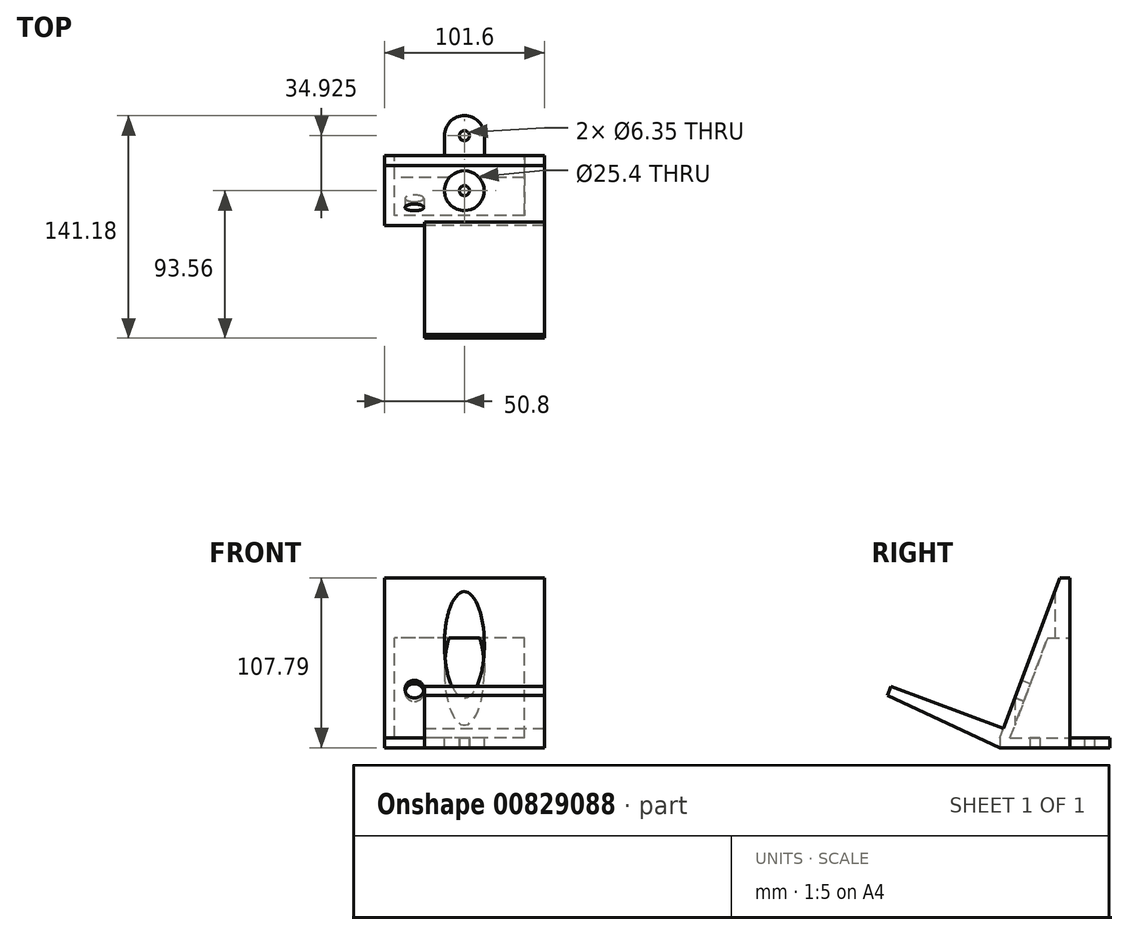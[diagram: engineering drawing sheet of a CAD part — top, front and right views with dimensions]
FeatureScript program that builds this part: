
annotation { "Feature Type Name" : "Feature", "Feature Type Description" : "" }
export const myFeature = defineFeature(function(context is Context, id is Id, definition is map)
    precondition{}
    {
        {
            var Q0;
            Q0=qCreatedBy(makeId("Right.planeOp"),FACE);
            var sketch = newSketch(context, id + "F0", { "sketchPlane" : qUnion([Q0])});
            skLineSegment(sketch, "E0.top", {"start": v(-30.3, 41.28) * mm, "end": v(14.14, 41.28) * mm});
            skLineSegment(sketch, "E0.left", {"start": v(-30.3, 47.63) * mm, "end": v(-30.3, 41.28) * mm});
            skLineSegment(sketch, "E0.right", {"start": v(14.14, 47.47) * mm, "end": v(14.14, 41.28) * mm});
            skLineSegment(sketch, "E1.top", {"start": v(14.14, 149.07) * mm, "end": v(7.8, 149.07) * mm});
            skLineSegment(sketch, "E1.left", {"start": v(14.14, 47.47) * mm, "end": v(14.14, 149.07) * mm});
            skLineSegment(sketch, "E2.left", {"start": v(14.14, 41.28) * mm, "end": v(14.14, 47.63) * mm});
            skLineSegment(sketch, "E3", {"start": v(-30.3, 47.63) * mm, "end": v(7.8, 149.07) * mm});
            skLineSegment(sketch, "E4", {"start": v(-5.62, 113.36) * mm, "end": v(0.33, 111.13) * mm, "construction": true});
            skLineSegment(sketch, "E5", {"start": v(-30.3, 47.63) * mm, "end": v(-101.64, 74.43) * mm});
            skLineSegment(sketch, "E6", {"start": v(-101.64, 74.43) * mm, "end": v(-99.4, 80.37) * mm});
            skLineSegment(sketch, "E7", {"start": v(-99.4, 80.37) * mm, "end": v(-28.07, 53.58) * mm});
            skLineSegment(sketch, "E8", {"start": v(-101.64, 74.43) * mm, "end": v(-30.3, 41.28) * mm});
            skLineSegment(sketch, "E9", {"start": v(-23.72, 47.63) * mm, "end": v(0.13, 111.13) * mm});
            skLineSegment(sketch, "E10", {"start": v(0.13, 111.13) * mm, "end": v(7.8, 111.13) * mm});
            skLineSegment(sketch, "E11", {"start": v(7.8, 111.13) * mm, "end": v(7.8, 47.63) * mm});
            skLineSegment(sketch, "E12", {"start": v(7.8, 47.63) * mm, "end": v(-23.72, 47.63) * mm});
            skLineSegment(sketch, "E13", {"start": v(-11.58, 47.63) * mm, "end": v(-11.58, 41.28) * mm, "construction": true});
            skLineSegment(sketch, "E14", {"start": v(7.8, 79.38) * mm, "end": v(14.14, 79.38) * mm, "construction": true});
            skSolve(sketch);
        }
        {
            var Q0;
            Q0=makeQuery(id+"F0.imprint","IMPRINT",FACE,{"disambiguationData":[TD([[makeQuery(id+"F0.imprint","IMPRINT",EDGE,{"derivedFrom":sQuery(id+"F0.wireOp",EDGE,"E1.bottom")}),-1.0]])]});
            var Q1;
            Q1=makeQuery(id+"F0.imprint","IMPRINT",FACE,{"disambiguationData":[TD([[makeQuery(id+"F0.imprint","IMPRINT",EDGE,{"derivedFrom":sQuery(id+"F0.wireOp",EDGE,"E0.top")}),1.0]])]});
            extrude(context, id + "F1", {"entities" : qUnion([Q0, Q1]), "depth" : 101.6 * mm, "offsetDistance" : 25.4 * mm});
        }
        {
            var Q0;
            Q0=makeQuery(id+"F1.opExtrude","CAP_FACE",FACE,{"disambiguationData":[OSD([sQuery(id+"F0.wireOp",EDGE,"E0.bottom"),sQuery(id+"F0.wireOp",EDGE,"E0.top"),sQuery(id+"F0.wireOp",EDGE,"E0.left"),sQuery(id+"F0.wireOp",EDGE,"E1.top"),sQuery(id+"F0.wireOp",EDGE,"E1.left"),sQuery(id+"F0.wireOp",EDGE,"E1.right"),sQuery(id+"F0.wireOp",EDGE,"E2.bottom"),sQuery(id+"F0.wireOp",EDGE,"E2.top"),sQuery(id+"F0.wireOp",EDGE,"E2.right"),sQuery(id+"F0.wireOp",EDGE,"E3"),sQuery(id+"F0.wireOp",EDGE,"QY4DRkzs-TfP7-npSZ-TyTt-AMgr2LJXPMgd")])],"isStart":false});
            var sketch = newSketch(context, id + "F2", { "sketchPlane" : qUnion([Q0])});
            skLineSegment(sketch, "E15", {"start": v(-30.3, 47.63) * mm, "end": v(-101.64, 74.43) * mm});
            skLineSegment(sketch, "E16", {"start": v(-102.26, 74.66) * mm, "end": v(-100.04, 80.57) * mm, "construction": true});
            skLineSegment(sketch, "E17", {"start": v(-100.04, 80.57) * mm, "end": v(-28.08, 53.54) * mm});
            skLineSegment(sketch, "E18", {"start": v(-10.32, 100.84) * mm, "end": v(-12.55, 94.9) * mm});
            skLineSegment(sketch, "E19", {"start": v(-28.08, 53.54) * mm, "end": v(7.64, 148.66) * mm, "construction": true});
            skLineSegment(sketch, "E20", {"start": v(-100.04, 80.57) * mm, "end": v(-101.64, 74.43) * mm});
            skLineSegment(sketch, "E21", {"start": v(-101.64, 74.43) * mm, "end": v(-30.3, 41.28) * mm});
            skLineSegment(sketch, "E22", {"start": v(-30.3, 41.28) * mm, "end": v(-30.3, 47.63) * mm});
            skSolve(sketch);
        }
        {
            var Q0;
            {var subQ0=sQuery(id+"F0.wireOp",EDGE,"E3");Q0=makeQuery(id+"F9g9BXxNrQaE6eR_1.boolean.opBoolean","MERGE",FACE,{"derivedFrom":[makeQuery(id+"F1.opExtrude","SWEPT_FACE",FACE,{"disambiguationData":[OSD([subQ0])]}),makeQuery(id+"F9g9BXxNrQaE6eR_1.opExtrude","SWEPT_FACE",FACE,{"disambiguationData":[OSD([subQ0]),TDD([makeQuery(id+"F0.imprint","IMPRINT",EDGE,{"derivedFrom":subQ0})])]})]});}
            var sketch = newSketch(context, id + "F3", { "sketchPlane" : qUnion([Q0])});
            skLineSegment(sketch, "E23", {"start": v(19.05, 33.93) * mm, "end": v(19.05, 66.95) * mm, "construction": true});
            skLineSegment(sketch, "E24", {"start": v(19.05, 66.95) * mm, "end": v(95.25, 66.95) * mm, "construction": true});
            skLineSegment(sketch, "E25", {"start": v(95.25, 66.95) * mm, "end": v(101.6, 66.95) * mm, "construction": true});
            skCircle(sketch, "E26", {"center": v(19.05, 66.95) * mm, "radius": 6 * mm});
            skLineSegment(sketch, "E27", {"start": v(13.07, 67.5) * mm, "end": v(6.35, 67.5) * mm, "construction": true});
            skSolve(sketch);
        }
        {
            var Q0;
            Q0=makeQuery(id+"F3.imprint","IMPRINT",FACE,{"disambiguationData":[TD([[makeQuery(id+"F3.imprint","IMPRINT",EDGE,{"derivedFrom":sQuery(id+"F3.wireOp",EDGE,"E26")}),1.0]])]});
            var Q1;
            Q1=makeQuery(id+"F3.imprint","IMPRINT",FACE,{"disambiguationData":[TD([[makeQuery(id+"F3.imprint","IMPRINT",EDGE,{"derivedFrom":sQuery(id+"F3.wireOp",EDGE,"cZBbjcpk-DuDn-rtNu-iiUc-7TDWmWub5VdI")}),1.0]])]});
            extrude(context, id + "F4", {"entities" : qUnion([Q0, Q1]), "operationType" : NewBodyOperationType.REMOVE, "oppositeDirection" : true, "depth" : 12.7 * mm, "offsetDistance" : 25.4 * mm});
        }
        {
            var Q0;
            Q0=makeQuery(id+"F1.opExtrude","CAP_FACE",FACE,{"disambiguationData":[OSD([sQuery(id+"F0.wireOp",EDGE,"E0.top"),sQuery(id+"F0.wireOp",EDGE,"E0.left"),sQuery(id+"F0.wireOp",EDGE,"E1.top"),sQuery(id+"F0.wireOp",EDGE,"E1.left"),sQuery(id+"F0.wireOp",EDGE,"E2.left"),sQuery(id+"F0.wireOp",EDGE,"E3"),sQuery(id+"F0.wireOp",EDGE,"E10"),sQuery(id+"F0.wireOp",EDGE,"E11"),sQuery(id+"F0.wireOp",EDGE,"E9"),sQuery(id+"F0.wireOp",EDGE,"E12")])],"isStart":false});
            var sketch = newSketch(context, id + "F5", { "sketchPlane" : qUnion([Q0])});
            skLineSegment(sketch, "E28", {"start": v(-30.3, 47.63) * mm, "end": v(-101.64, 74.43) * mm});
            skLineSegment(sketch, "E29", {"start": v(-101.64, 74.43) * mm, "end": v(-99.4, 80.37) * mm});
            skLineSegment(sketch, "E30", {"start": v(-99.4, 80.37) * mm, "end": v(-28.07, 53.58) * mm});
            skLineSegment(sketch, "E31", {"start": v(-101.64, 74.43) * mm, "end": v(-30.3, 41.28) * mm});
            skLineSegment(sketch, "E32", {"start": v(-30.3, 41.28) * mm, "end": v(-30.3, 47.63) * mm});
            skSolve(sketch);
        }
        {
            var Q0;
            {var subQ0=sQuery(id+"F5.wireOp",EDGE,"E28");Q0=makeQuery(id+"F5.imprint","IMPRINT",FACE,{"disambiguationData":[TD([[makeQuery(id+"F5.imprint","IMPRINT",EDGE,{"derivedFrom":subQ0}),-1.0]])]});}
            var Q1;
            Q1=makeQuery(id+"F5.imprint","IMPRINT",FACE,{"disambiguationData":[TD([[makeQuery(id+"F5.imprint","IMPRINT",EDGE,{"derivedFrom":sQuery(id+"F5.wireOp",EDGE,"E28")}),1.0]])]});
            extrude(context, id + "F6", {"entities" : qUnion([Q0, Q1]), "operationType" : NewBodyOperationType.ADD, "oppositeDirection" : true, "depth" : 76.2 * mm, "offsetDistance" : 25.4 * mm});
        }
        {
            var Q0;
            {var subQ0=sQuery(id+"F0.wireOp",EDGE,"E3");Q0=makeQuery(id+"F6.boolean.opBoolean","MERGE",FACE,{"derivedFrom":[makeQuery(id+"F1.opExtrude","CAP_FACE",FACE,{"disambiguationData":[OSD([sQuery(id+"F0.wireOp",EDGE,"E0.top"),sQuery(id+"F0.wireOp",EDGE,"E0.left"),sQuery(id+"F0.wireOp",EDGE,"E1.top"),sQuery(id+"F0.wireOp",EDGE,"E1.left"),sQuery(id+"F0.wireOp",EDGE,"E2.left"),subQ0,sQuery(id+"F0.wireOp",EDGE,"E10"),sQuery(id+"F0.wireOp",EDGE,"E11"),sQuery(id+"F0.wireOp",EDGE,"E9"),sQuery(id+"F0.wireOp",EDGE,"E12")])],"isStart":false}),makeQuery(id+"F6.opExtrude","CAP_FACE",FACE,{"disambiguationData":[OSD([subQ0,sQuery(id+"F5.wireOp",EDGE,"E29"),sQuery(id+"F5.wireOp",EDGE,"E30"),sQuery(id+"F5.wireOp",EDGE,"E31"),sQuery(id+"F5.wireOp",EDGE,"E32")])],"isStart":true})]});}
            var sketch = newSketch(context, id + "F7", { "sketchPlane" : qUnion([Q0])});
            skLineSegment(sketch, "E33", {"start": v(7.8, 47.63) * mm, "end": v(-23.72, 47.63) * mm});
            skLineSegment(sketch, "E34", {"start": v(-23.72, 47.63) * mm, "end": v(0.13, 111.13) * mm});
            skLineSegment(sketch, "E35", {"start": v(0.13, 111.13) * mm, "end": v(7.8, 111.13) * mm});
            skLineSegment(sketch, "E36", {"start": v(7.8, 111.13) * mm, "end": v(7.8, 47.63) * mm});
            skSolve(sketch);
        }
        {
            var Q0;
            Q0=makeQuery(id+"F7.imprint","IMPRINT",FACE,{"disambiguationData":[TD([[makeQuery(id+"F7.imprint","IMPRINT",EDGE,{"derivedFrom":sQuery(id+"F7.wireOp",EDGE,"E33")}),-1.0]])]});
            extrude(context, id + "F8", {"entities" : qUnion([Q0]), "operationType" : NewBodyOperationType.ADD, "oppositeDirection" : true, "depth" : 12.7 * mm, "offsetDistance" : 25.4 * mm});
        }
        {
            var Q0;
            Q0=makeQuery(id+"F1.opExtrude","SWEPT_FACE",FACE,{"disambiguationData":[OSD([sQuery(id+"F0.wireOp",EDGE,"E1.left"),sQuery(id+"F0.wireOp",EDGE,"E2.left")])]});
            var sketch = newSketch(context, id + "F9", { "sketchPlane" : qUnion([Q0])});
            skLineSegment(sketch, "E37", {"start": v(-88.9, 41.28) * mm, "end": v(-88.9, 47.63) * mm, "construction": true});
            skLineSegment(sketch, "E38", {"start": v(-101.6, 47.63) * mm, "end": v(-88.9, 47.63) * mm, "construction": true});
            skLineSegment(sketch, "E39", {"start": v(0, 105.57) * mm, "end": v(-6.35, 105.57) * mm, "construction": true});
            skLineSegment(sketch, "E40.bottom", {"start": v(-88.9, 47.63) * mm, "end": v(-6.35, 47.63) * mm});
            skLineSegment(sketch, "E40.top", {"start": v(-88.9, 111.13) * mm, "end": v(-6.35, 111.13) * mm});
            skLineSegment(sketch, "E40.left", {"start": v(-88.9, 47.63) * mm, "end": v(-88.9, 111.13) * mm});
            skLineSegment(sketch, "E40.right", {"start": v(-6.35, 47.63) * mm, "end": v(-6.35, 111.13) * mm});
            skSolve(sketch);
        }
        {
            var Q0;
            Q0=makeQuery(id+"F9.imprint","IMPRINT",FACE,{"disambiguationData":[TD([[makeQuery(id+"F9.imprint","IMPRINT",EDGE,{"derivedFrom":sQuery(id+"F9.wireOp",EDGE,"E40.bottom")}),1.0]])]});
            extrude(context, id + "F10", {"entities" : qUnion([Q0]), "operationType" : NewBodyOperationType.REMOVE, "endBound" : BoundingType.UP_TO_NEXT, "oppositeDirection" : true, "depth" : 10.92 * mm, "offsetDistance" : 25.4 * mm});
        }
        {
            var Q0;
            Q0=makeQuery(id+"F1.opExtrude","CAP_FACE",FACE,{"disambiguationData":[OSD([sQuery(id+"F0.wireOp",EDGE,"E0.top"),sQuery(id+"F0.wireOp",EDGE,"E0.left"),sQuery(id+"F0.wireOp",EDGE,"E1.top"),sQuery(id+"F0.wireOp",EDGE,"E1.left"),sQuery(id+"F0.wireOp",EDGE,"E2.left"),sQuery(id+"F0.wireOp",EDGE,"E3"),sQuery(id+"F0.wireOp",EDGE,"E10"),sQuery(id+"F0.wireOp",EDGE,"E11"),sQuery(id+"F0.wireOp",EDGE,"E9"),sQuery(id+"F0.wireOp",EDGE,"E12")])],"isStart":true});
            var sketch = newSketch(context, id + "F11", { "sketchPlane" : qUnion([Q0])});
            skLineSegment(sketch, "E41", {"start": v(-7.8, 111.13) * mm, "end": v(-7.8, 47.63) * mm});
            skLineSegment(sketch, "E42", {"start": v(-7.8, 47.63) * mm, "end": v(23.72, 47.63) * mm});
            skLineSegment(sketch, "E43", {"start": v(23.72, 47.63) * mm, "end": v(-0.13, 111.13) * mm});
            skLineSegment(sketch, "E44", {"start": v(-0.13, 111.13) * mm, "end": v(-7.8, 111.13) * mm});
            skSolve(sketch);
        }
        {
            var Q0;
            Q0=makeQuery(id+"F1.opExtrude","SWEPT_FACE",FACE,{"disambiguationData":[OSD([sQuery(id+"F0.wireOp",EDGE,"E0.top")])]});
            var sketch = newSketch(context, id + "F12", { "sketchPlane" : qUnion([Q0])});
            skCircle(sketch, "E45", {"center": v(50.8, 8.08) * mm, "radius": 3.18 * mm});
            skLineSegment(sketch, "E46", {"start": v(50.8, -14.14) * mm, "end": v(50.8, 8.08) * mm, "construction": true});
            skLineSegment(sketch, "E47", {"start": v(50.8, 30.3) * mm, "end": v(50.8, 8.08) * mm, "construction": true});
            skLineSegment(sketch, "E48", {"start": v(50.8, 8.08) * mm, "end": v(0, 8.08) * mm, "construction": true});
            skLineSegment(sketch, "E49", {"start": v(50.8, 8.08) * mm, "end": v(101.6, 8.08) * mm, "construction": true});
            skSolve(sketch);
        }
        {
            var Q0;
            Q0=makeQuery(id+"F12.imprint","IMPRINT",FACE,{"disambiguationData":[TD([[makeQuery(id+"F12.imprint","IMPRINT",EDGE,{"derivedFrom":sQuery(id+"F12.wireOp",EDGE,"E45")}),1.0]])]});
            extrude(context, id + "F13", {"entities" : qUnion([Q0]), "operationType" : NewBodyOperationType.REMOVE, "oppositeDirection" : true, "depth" : 25.4 * mm, "offsetDistance" : 25.4 * mm});
        }
        {
            var Q0;
            Q0=makeQuery(id+"F11.imprint","IMPRINT",FACE,{"disambiguationData":[TD([[makeQuery(id+"F11.imprint","IMPRINT",EDGE,{"derivedFrom":sQuery(id+"F11.wireOp",EDGE,"E41")}),1.0]])]});
            extrude(context, id + "F14", {"entities" : qUnion([Q0]), "operationType" : NewBodyOperationType.ADD, "oppositeDirection" : true, "depth" : 6.35 * mm, "offsetDistance" : 25.4 * mm});
        }
        {
            var Q0;
            Q0=makeQuery(id+"F10.boolean.opBoolean","MERGE",FACE,{"derivedFrom":[makeQuery(id+"F1.opExtrude","SWEPT_FACE",FACE,{"disambiguationData":[OSD([sQuery(id+"F0.wireOp",EDGE,"E12")])]}),makeQuery(id+"F10.opExtrude","SWEPT_FACE",FACE,{"disambiguationData":[OSD([sQuery(id+"F9.wireOp",EDGE,"E40.bottom")])]})]});
            var sketch = newSketch(context, id + "F15", { "sketchPlane" : qUnion([Q0])});
            skCircle(sketch, "E50", {"center": v(50.8, -8.08) * mm, "radius": 12.7 * mm});
            skCircle(sketch, "E51", {"center": v(50.8, 26.84) * mm, "radius": 12.7 * mm});
            skLineSegment(sketch, "E52", {"start": v(50.8, -8.08) * mm, "end": v(50.8, 37.16) * mm, "construction": true});
            skLineSegment(sketch, "E53", {"start": v(63.5, 26.84) * mm, "end": v(63.5, 14.14) * mm});
            skLineSegment(sketch, "E54", {"start": v(38.1, 26.84) * mm, "end": v(38.1, 14.14) * mm});
            skCircle(sketch, "E55", {"center": v(50.8, 26.84) * mm, "radius": 3.18 * mm});
            skSolve(sketch);
        }
        {
            var Q0;
            Q0=makeQuery(id+"F15.imprint","IMPRINT",FACE,{"disambiguationData":[TD([[makeQuery(id+"F15.imprint","IMPRINT",EDGE,{"derivedFrom":sQuery(id+"F15.wireOp",EDGE,"E50")}),1.0]])]});
            var Q1;
            Q1=makeQuery(id+"F15.imprint","IMPRINT",FACE,{"disambiguationData":[TD([[makeQuery(id+"F15.imprint","IMPRINT",EDGE,{"derivedFrom":makeQuery(id+"F13.boolean.opBoolean","INTERSECT",EDGE,{"derivedFrom":[makeQuery(id+"F10.boolean.opBoolean","MERGE",FACE,{"derivedFrom":[makeQuery(id+"F1.opExtrude","SWEPT_FACE",FACE,{"disambiguationData":[OSD([sQuery(id+"F0.wireOp",EDGE,"E12")])]}),makeQuery(id+"F10.opExtrude","SWEPT_FACE",FACE,{"disambiguationData":[OSD([sQuery(id+"F9.wireOp",EDGE,"E40.bottom")])]})]}),makeQuery(id+"F13.opExtrude","SWEPT_FACE",FACE,{"disambiguationData":[OSD([sQuery(id+"F12.wireOp",EDGE,"E45")])]})]})}),-1.0]])]});
            extrude(context, id + "F16", {"entities" : qUnion([Q0, Q1]), "operationType" : NewBodyOperationType.REMOVE, "depth" : 127 * mm, "offsetDistance" : 25.4 * mm});
        }
        {
            var Q0;
            Q0=makeQuery(id+"F15.imprint","IMPRINT",FACE,{"disambiguationData":[TD([[makeQuery(id+"F15.imprint","IMPRINT",EDGE,{"derivedFrom":sQuery(id+"F15.wireOp",EDGE,"E55")}),-1.0]])]});
            var Q1;
            {var subQ0=sQuery(id+"F15.wireOp",EDGE,"E53");Q1=makeQuery(id+"F15.imprint","IMPRINT",FACE,{"disambiguationData":[TD([[makeQuery(id+"F15.imprint","IMPRINT",EDGE,{"derivedFrom":subQ0}),-1.0]])]});}
            var Q2;
            {var subQ0=sQuery(id+"F15.wireOp",EDGE,"E54");Q2=makeQuery(id+"F15.imprint","IMPRINT",FACE,{"disambiguationData":[TD([[makeQuery(id+"F15.imprint","IMPRINT",EDGE,{"derivedFrom":subQ0}),1.0]])]});}
            extrude(context, id + "F17", {"entities" : qUnion([Q0, Q1, Q2]), "operationType" : NewBodyOperationType.ADD, "oppositeDirection" : true, "depth" : 6.35 * mm, "offsetDistance" : 25.4 * mm});
        }
    });
